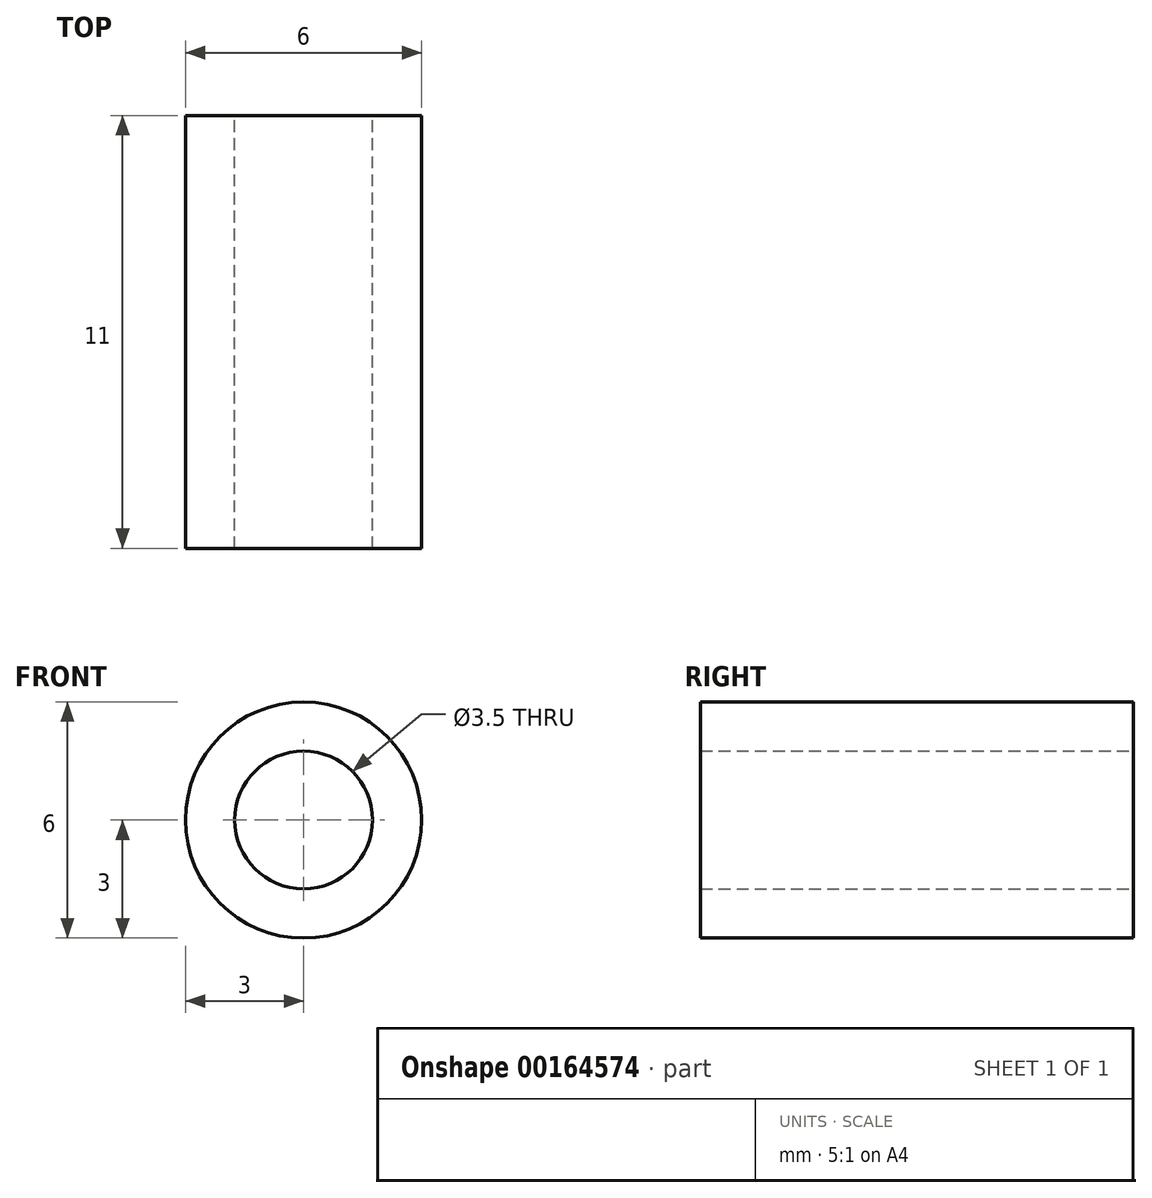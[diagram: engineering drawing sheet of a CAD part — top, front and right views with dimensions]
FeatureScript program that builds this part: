
annotation { "Feature Type Name" : "Feature", "Feature Type Description" : "" }
export const myFeature = defineFeature(function(context is Context, id is Id, definition is map)
    precondition{}
    {
        {
            var Q0;
            Q0=qCreatedBy(makeId("Front.planeOp"),FACE);
            var sketch = newSketch(context, id + "F0", { "sketchPlane" : qUnion([Q0])});
            skCircle(sketch, "E0", {"center": v(0, 0) * mm, "radius": 1.75 * mm});
            skCircle(sketch, "E1", {"center": v(0, 0) * mm, "radius": 3 * mm});
            skSolve(sketch);
        }
        {
            var Q0;
            Q0 = qSketchRegion(id + "F0", true);
            extrude(context, id + "F1", {"entities" : qUnion([Q0]), "depth" : 11 * mm});
        }
    });
